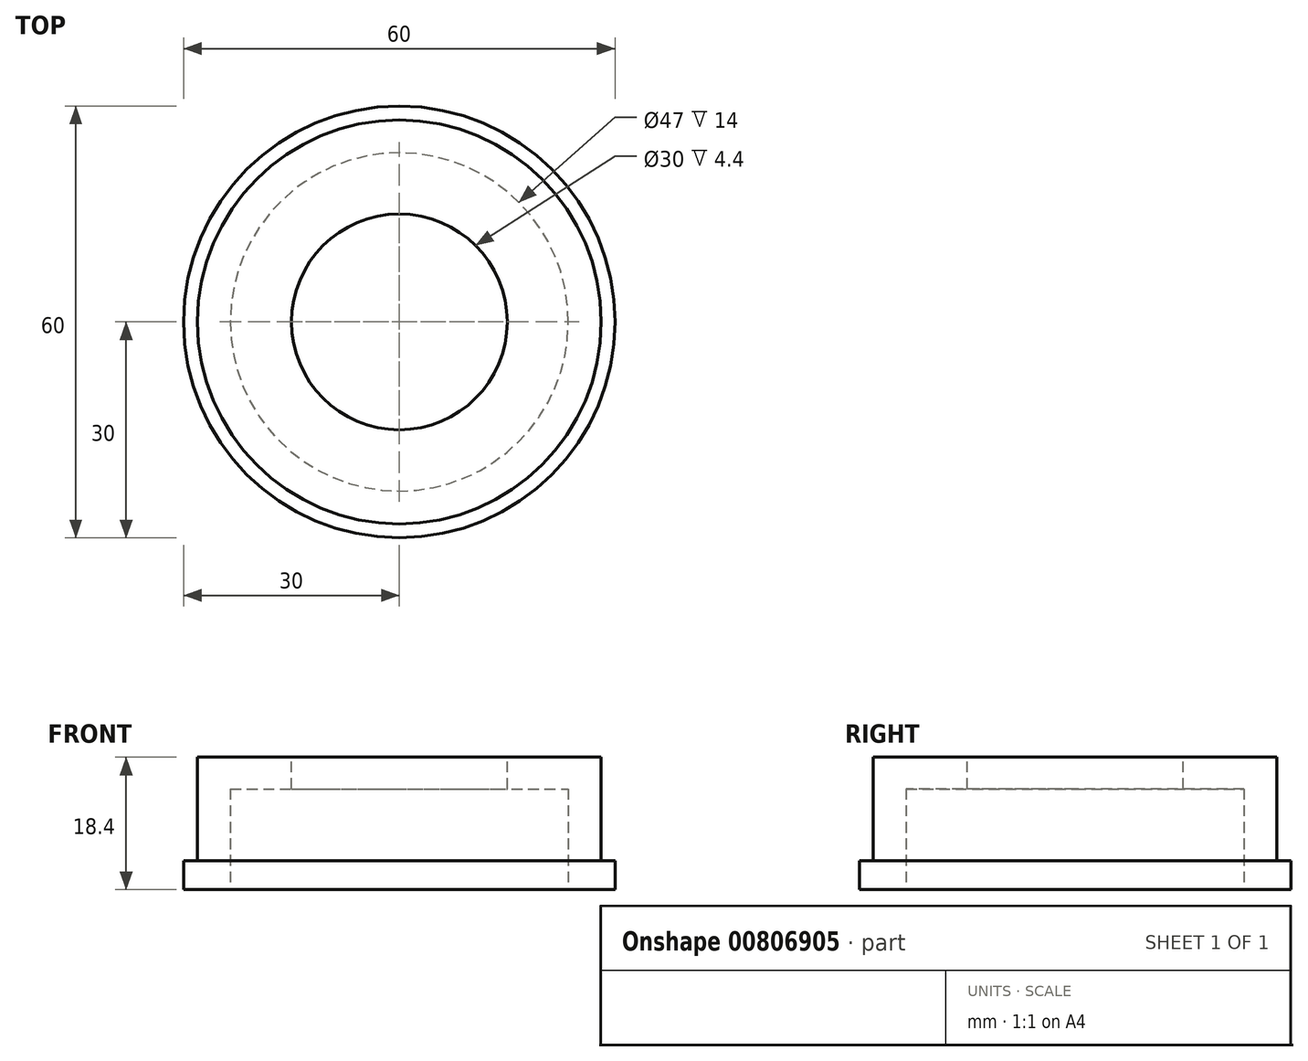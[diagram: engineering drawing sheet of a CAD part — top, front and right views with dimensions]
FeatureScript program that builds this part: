
annotation { "Feature Type Name" : "Feature", "Feature Type Description" : "" }
export const myFeature = defineFeature(function(context is Context, id is Id, definition is map)
    precondition{}
    {
        {
            var Q0;
            Q0=qCreatedBy(makeId("Top.planeOp"),FACE);
            var sketch = newSketch(context, id + "F0", { "sketchPlane" : qUnion([Q0])});
            skCircle(sketch, "E0", {"center": v(0, 0) * mm, "radius": 30 * mm});
            skSolve(sketch);
        }
        {
            var Q0;
            Q0 = qSketchRegion(id + "F0", true);
            extrude(context, id + "F1", {"entities" : qUnion([Q0]), "depth" : 4 * mm, "offsetDistance" : 25 * mm});
        }
        {
            var Q0;
            Q0=makeQuery(id+"F1.opExtrude","CAP_FACE",FACE,{"disambiguationData":[OSD([sQuery(id+"F0.wireOp",EDGE,"E0")])],"isStart":false});
            var sketch = newSketch(context, id + "F2", { "sketchPlane" : qUnion([Q0])});
            skCircle(sketch, "E1", {"center": v(0, 0) * mm, "radius": 28.07 * mm});
            skSolve(sketch);
        }
        {
            var Q0;
            Q0=makeQuery(id+"F2.imprint","IMPRINT",FACE,{"disambiguationData":[TD([[makeQuery(id+"F2.imprint","IMPRINT",EDGE,{"derivedFrom":sQuery(id+"F2.wireOp",EDGE,"E1")}),1.0]])]});
            extrude(context, id + "F3", {"entities" : qUnion([Q0]), "operationType" : NewBodyOperationType.ADD, "depth" : 14.4 * mm, "offsetDistance" : 25 * mm});
        }
        {
            var Q0;
            Q0=makeQuery(id+"F1.opExtrude","CAP_FACE",FACE,{"disambiguationData":[OSD([sQuery(id+"F0.wireOp",EDGE,"E0")])],"isStart":true});
            var sketch = newSketch(context, id + "F4", { "sketchPlane" : qUnion([Q0])});
            skCircle(sketch, "E2", {"center": v(0, 0) * mm, "radius": 23.5 * mm});
            skSolve(sketch);
        }
        {
            var Q0;
            Q0=makeQuery(id+"F4.imprint","IMPRINT",FACE,{"disambiguationData":[TD([[makeQuery(id+"F4.imprint","IMPRINT",EDGE,{"derivedFrom":sQuery(id+"F4.wireOp",EDGE,"E2")}),1.0]])]});
            extrude(context, id + "F5", {"entities" : qUnion([Q0]), "operationType" : NewBodyOperationType.REMOVE, "oppositeDirection" : true, "depth" : 14 * mm, "offsetDistance" : 25 * mm});
        }
        {
            var Q0;
            Q0=makeQuery(id+"F3.opExtrude","CAP_FACE",FACE,{"disambiguationData":[OSD([sQuery(id+"F2.wireOp",EDGE,"E1")])],"isStart":false});
            var sketch = newSketch(context, id + "F6", { "sketchPlane" : qUnion([Q0])});
            skCircle(sketch, "E3", {"center": v(0, 0) * mm, "radius": 15 * mm});
            skSolve(sketch);
        }
        {
            var Q0;
            Q0=makeQuery(id+"F6.imprint","IMPRINT",FACE,{"disambiguationData":[TD([[makeQuery(id+"F6.imprint","IMPRINT",EDGE,{"derivedFrom":sQuery(id+"F6.wireOp",EDGE,"E3")}),1.0]])]});
            extrude(context, id + "F7", {"entities" : qUnion([Q0]), "operationType" : NewBodyOperationType.REMOVE, "endBound" : BoundingType.THROUGH_ALL, "oppositeDirection" : true, "depth" : 25 * mm, "offsetDistance" : 25 * mm});
        }
    });
